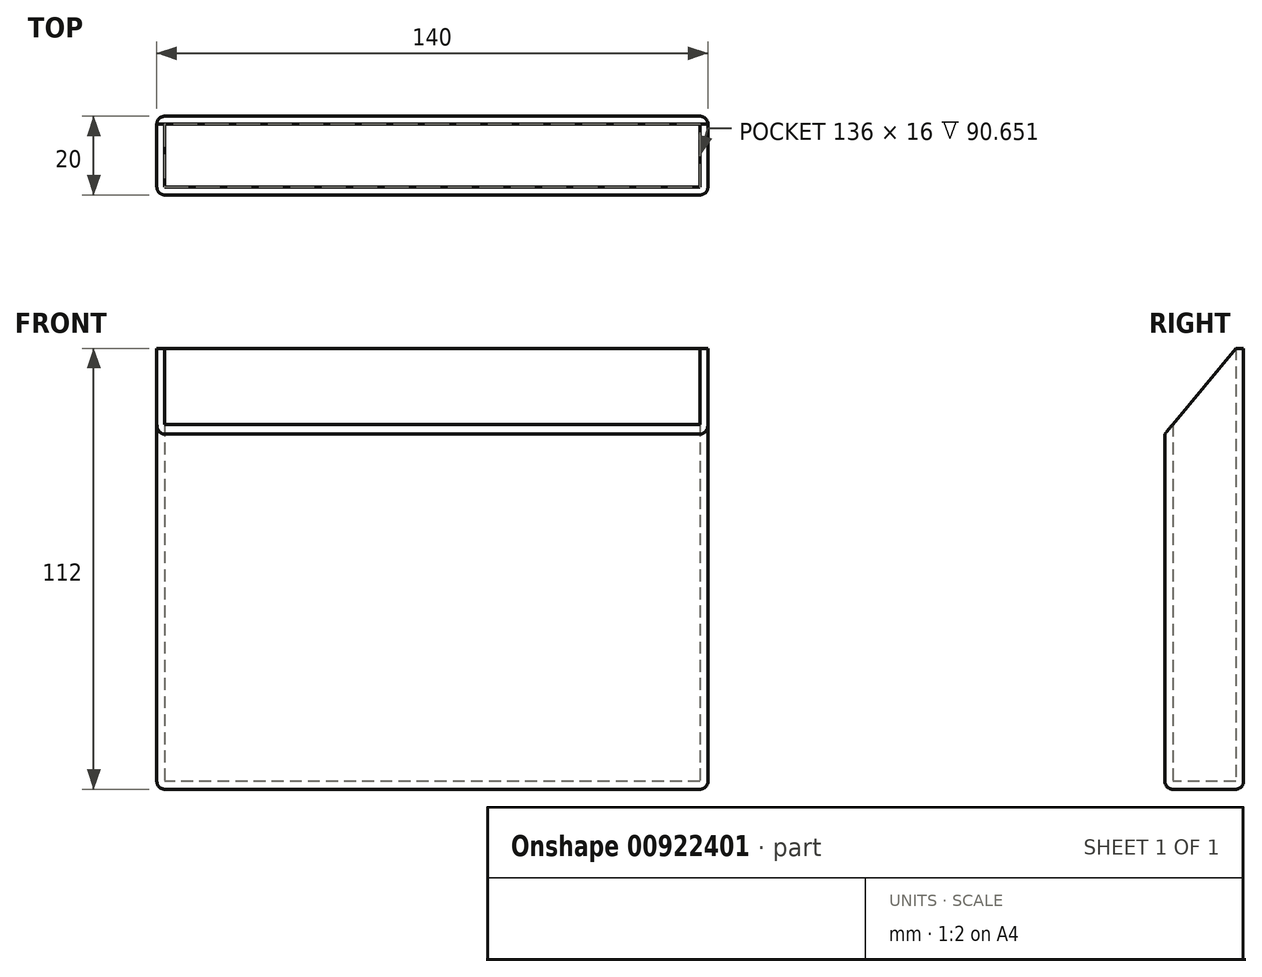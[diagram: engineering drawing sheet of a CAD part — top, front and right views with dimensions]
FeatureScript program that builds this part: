
annotation { "Feature Type Name" : "Feature", "Feature Type Description" : "" }
export const myFeature = defineFeature(function(context is Context, id is Id, definition is map)
    precondition{}
    {
        {
            var Q0;
            Q0=qCreatedBy(makeId("Top.planeOp"),FACE);
            var sketch = newSketch(context, id + "F0", { "sketchPlane" : qUnion([Q0])});
            skLineSegment(sketch, "E0.bottom", {"start": v(70, 10) * mm, "end": v(-70, 10) * mm});
            skLineSegment(sketch, "E0.top", {"start": v(70, -10) * mm, "end": v(-70, -10) * mm});
            skLineSegment(sketch, "E0.left", {"start": v(70, 10) * mm, "end": v(70, -10) * mm});
            skLineSegment(sketch, "E0.right", {"start": v(-70, 10) * mm, "end": v(-70, -10) * mm});
            skPoint(sketch, "E0.middle", {"position": v(0, 0) * mm});
            skSolve(sketch);
        }
        {
            var Q0;
            Q0 = qSketchRegion(id + "F0", true);
            extrude(context, id + "F1", {"entities" : qUnion([Q0]), "depth" : 2 * mm, "offsetDistance" : 25 * mm});
        }
        {
            var Q0;
            Q0=makeQuery(id+"F1.opExtrude","CAP_FACE",FACE,{"disambiguationData":[OSD([sQuery(id+"F0.wireOp",EDGE,"E0.bottom"),sQuery(id+"F0.wireOp",EDGE,"E0.top"),sQuery(id+"F0.wireOp",EDGE,"E0.left"),sQuery(id+"F0.wireOp",EDGE,"E0.right")])],"isStart":false});
            var sketch = newSketch(context, id + "F2", { "sketchPlane" : qUnion([Q0])});
            skLineSegment(sketch, "E1.0", {"start": v(-68, 8) * mm, "end": v(-68, -8) * mm});
            skLineSegment(sketch, "E1.1", {"start": v(68, 8) * mm, "end": v(-68, 8) * mm});
            skLineSegment(sketch, "E1.2", {"start": v(68, 8) * mm, "end": v(68, -8) * mm});
            skLineSegment(sketch, "E1.3", {"start": v(68, -8) * mm, "end": v(-68, -8) * mm});
            skSolve(sketch);
        }
        {
            var Q0;
            Q0=makeQuery(id+"F2.imprint","IMPRINT",FACE,{"disambiguationData":[TD([[makeQuery(id+"F2.imprint","IMPRINT",EDGE,{"derivedFrom":sQuery(id+"F2.wireOp",EDGE,"E1.0")}),-1.0]])]});
            extrude(context, id + "F3", {"entities" : qUnion([Q0]), "operationType" : NewBodyOperationType.ADD, "depth" : 110 * mm, "offsetDistance" : 25 * mm});
        }
        {
            var Q0;
            {var subQ0=sQuery(id+"F0.wireOp",EDGE,"E0.right");Q0=makeQuery(id+"F3.boolean.opBoolean","MERGE",FACE,{"derivedFrom":[makeQuery(id+"F1.opExtrude","SWEPT_FACE",FACE,{"disambiguationData":[OSD([subQ0])]}),makeQuery(id+"F3.opExtrude","SWEPT_FACE",FACE,{"disambiguationData":[OSD([subQ0])]})]});}
            var sketch = newSketch(context, id + "F4", { "sketchPlane" : qUnion([Q0])});
            skLineSegment(sketch, "E2", {"start": v(-8, 112) * mm, "end": v(10, 90.23) * mm});
            skPoint(sketch, "E3", {"position": v(-10, 112) * mm});
            skSolve(sketch);
        }
        {
            var Q0;
            Q0 = qSketchRegion(id + "F4", true);
            var Q1;
            {var subQ0=sQuery(id+"F4.wireOp",EDGE,"E2");Q1=makeQuery(id+"F4.imprint","IMPRINT",FACE,{"disambiguationData":[TD([[makeQuery(id+"F4.imprint","IMPRINT",EDGE,{"derivedFrom":subQ0}),1.0]])]});}
            extrude(context, id + "F5", {"entities" : qUnion([Q0, Q1]), "operationType" : NewBodyOperationType.REMOVE, "oppositeDirection" : true, "depth" : 160 * mm, "offsetDistance" : 25 * mm});
        }
        {
            var Q0;
            {var subQ0=sQuery(id+"F0.wireOp",EDGE,"E0.right");var subQ1=sQuery(id+"F0.wireOp",EDGE,"E0.top");Q0=makeQuery(id+"F3.boolean.opBoolean","MERGE",EDGE,{"derivedFrom":[makeQuery(id+"F1.opExtrude","SWEPT_EDGE",EDGE,{"disambiguationData":[OSD([subQ1,subQ0])]}),makeQuery(id+"F3.opExtrude","SWEPT_EDGE",EDGE,{"disambiguationData":[OSD([subQ1,subQ0])]})]});}
            var Q1;
            {var subQ0=sQuery(id+"F0.wireOp",EDGE,"E0.left");var subQ1=sQuery(id+"F0.wireOp",EDGE,"E0.top");Q1=makeQuery(id+"F3.boolean.opBoolean","MERGE",EDGE,{"derivedFrom":[makeQuery(id+"F1.opExtrude","SWEPT_EDGE",EDGE,{"disambiguationData":[OSD([subQ1,subQ0])]}),makeQuery(id+"F3.opExtrude","SWEPT_EDGE",EDGE,{"disambiguationData":[OSD([subQ1,subQ0])]})]});}
            var Q2;
            {var subQ0=sQuery(id+"F0.wireOp",EDGE,"E0.right");var subQ1=sQuery(id+"F0.wireOp",EDGE,"E0.bottom");Q2=makeQuery(id+"F3.boolean.opBoolean","MERGE",EDGE,{"derivedFrom":[makeQuery(id+"F1.opExtrude","SWEPT_EDGE",EDGE,{"disambiguationData":[OSD([subQ1,subQ0])]}),makeQuery(id+"F3.opExtrude","SWEPT_EDGE",EDGE,{"disambiguationData":[OSD([subQ1,subQ0])]})]});}
            var Q3;
            {var subQ0=sQuery(id+"F0.wireOp",EDGE,"E0.left");var subQ1=sQuery(id+"F0.wireOp",EDGE,"E0.bottom");Q3=makeQuery(id+"F3.boolean.opBoolean","MERGE",EDGE,{"derivedFrom":[makeQuery(id+"F1.opExtrude","SWEPT_EDGE",EDGE,{"disambiguationData":[OSD([subQ1,subQ0])]}),makeQuery(id+"F3.opExtrude","SWEPT_EDGE",EDGE,{"disambiguationData":[OSD([subQ1,subQ0])]})]});}
            var Q4;
            Q4=makeQuery(id+"F1.opExtrude","CAP_EDGE",EDGE,{"disambiguationData":[OSD([sQuery(id+"F0.wireOp",EDGE,"E0.top")])],"isStart":true});
            var Q5;
            Q5=makeQuery(id+"F1.opExtrude","CAP_EDGE",EDGE,{"disambiguationData":[OSD([sQuery(id+"F0.wireOp",EDGE,"E0.left")])],"isStart":true});
            var Q6;
            Q6=makeQuery(id+"F1.opExtrude","CAP_EDGE",EDGE,{"disambiguationData":[OSD([sQuery(id+"F0.wireOp",EDGE,"E0.bottom")])],"isStart":true});
            var Q7;
            Q7=makeQuery(id+"F1.opExtrude","CAP_EDGE",EDGE,{"disambiguationData":[OSD([sQuery(id+"F0.wireOp",EDGE,"E0.right")])],"isStart":true});
            fillet(context, id + "F6", {"entities" : qUnion([Q0, Q1, Q2, Q3, Q4, Q5, Q6, Q7]), "radius" : 2 * mm, "tangentPropagation" : true, "allowEdgeOverflow" : false});
        }
    });
